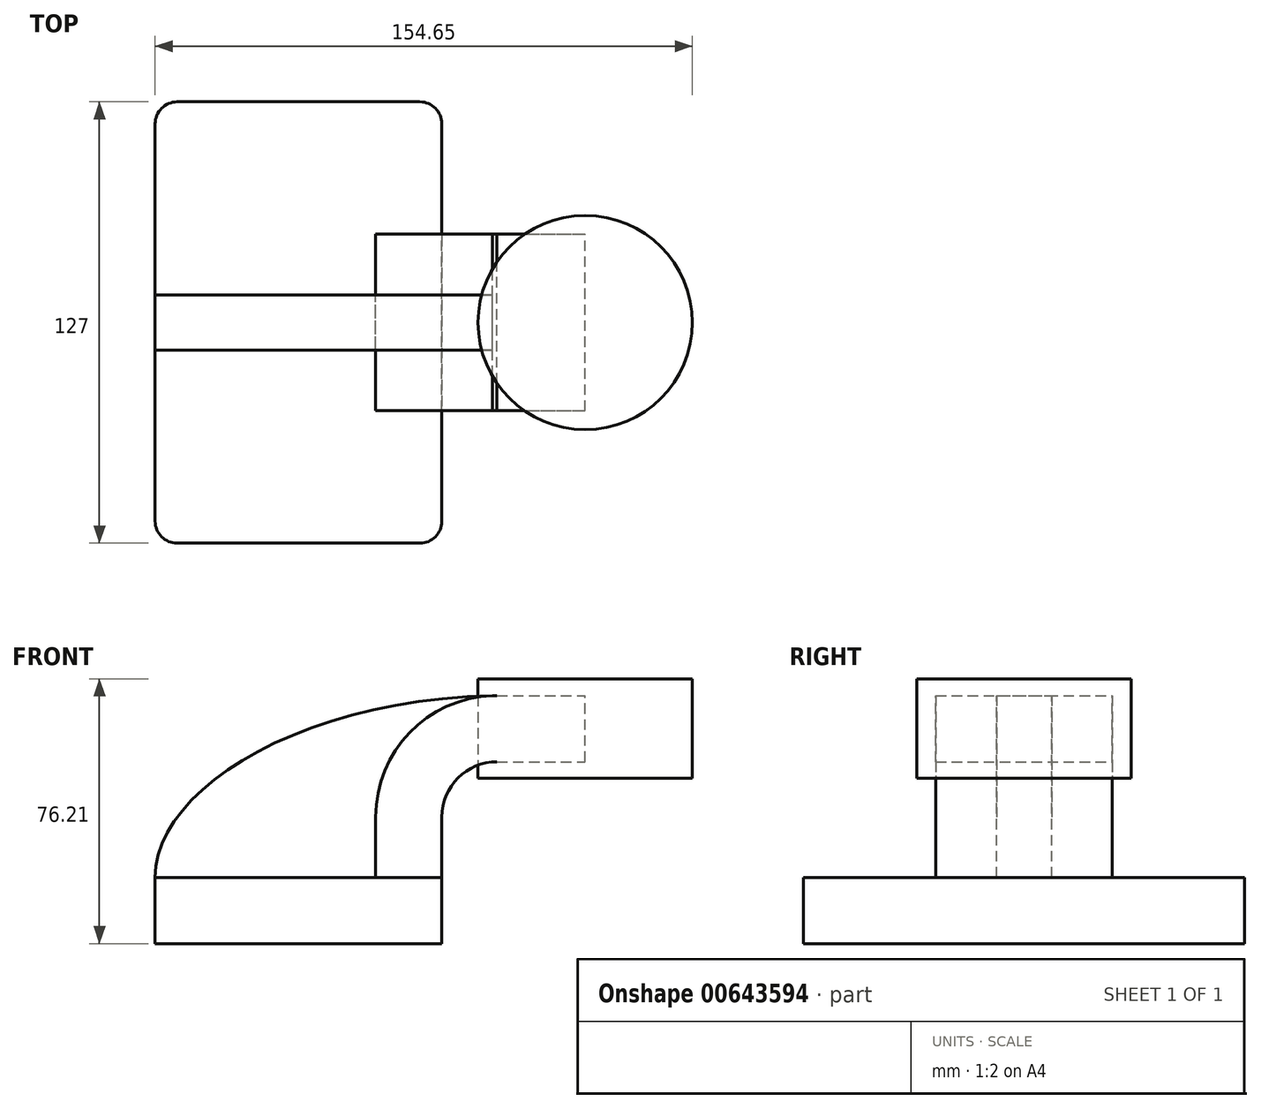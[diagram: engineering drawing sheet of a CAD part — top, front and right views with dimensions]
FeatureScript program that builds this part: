
annotation { "Feature Type Name" : "Feature", "Feature Type Description" : "" }
export const myFeature = defineFeature(function(context is Context, id is Id, definition is map)
    precondition{}
    {
        {
            var Q0;
            Q0=qCreatedBy(makeId("Front.planeOp"),FACE);
            var sketch = newSketch(context, id + "F0", { "sketchPlane" : qUnion([Q0])});
            skLineSegment(sketch, "E0.bottom", {"start": v(-41.28, 9.52) * mm, "end": v(41.27, 9.53) * mm});
            skLineSegment(sketch, "E0.top", {"start": v(-41.28, -9.53) * mm, "end": v(41.28, -9.53) * mm});
            skLineSegment(sketch, "E0.left", {"start": v(-41.28, 9.52) * mm, "end": v(-41.28, -9.53) * mm});
            skLineSegment(sketch, "E0.right", {"start": v(41.27, 9.53) * mm, "end": v(41.28, -9.52) * mm});
            skPoint(sketch, "E0.middle", {"position": v(0, 0) * mm});
            skLineSegment(sketch, "E1.bottom", {"start": v(62.57, 38.1) * mm, "end": v(113.37, 38.1) * mm});
            skLineSegment(sketch, "E1.top", {"start": v(62.57, 66.68) * mm, "end": v(113.37, 66.68) * mm});
            skLineSegment(sketch, "E1.left", {"start": v(62.57, 38.1) * mm, "end": v(62.57, 66.68) * mm});
            skLineSegment(sketch, "E1.right", {"start": v(113.37, 38.1) * mm, "end": v(113.37, 66.68) * mm});
            skPoint(sketch, "E1.middle", {"position": v(87.97, 52.39) * mm});
            skLineSegment(sketch, "E2", {"start": v(41.27, 9.53) * mm, "end": v(41.27, 26.92) * mm});
            skArc(sketch, "E3", {"start": v(41.27, 26.92) * mm, "mid": v(45.92, 38.15) * mm, "end": v(57.15, 42.8) * mm});
            skLineSegment(sketch, "E4", {"start": v(57.15, 42.8) * mm, "end": v(82.53, 42.8) * mm});
            skLineSegment(sketch, "E5.0", {"start": v(57.15, 61.85) * mm, "end": v(82.53, 61.85) * mm});
            skArc(sketch, "E5.1", {"start": v(22.22, 26.92) * mm, "mid": v(32.45, 51.62) * mm, "end": v(57.15, 61.85) * mm});
            skLineSegment(sketch, "E5.2", {"start": v(22.22, 9.53) * mm, "end": v(22.22, 26.92) * mm});
            skLineSegment(sketch, "E6", {"start": v(82.53, 38.1) * mm, "end": v(82.53, 66.68) * mm});
            skFitSpline(sketch, "E7", {"points": [v(-41.28, 9.52) * mm, v(57.15, 61.85) * mm], "startDerivative": vector(-0.56, 74.63) * mm, "endDerivative": vector(171.45, 2.65) * mm});
            skSolve(sketch);
        }
        {
            var Q0;
            Q0=makeQuery(id+"F0.imprint","IMPRINT",FACE,{"disambiguationData":[TD([[makeQuery(id+"F0.imprint","IMPRINT",EDGE,{"derivedFrom":sQuery(id+"F0.wireOp",EDGE,"E0.top")}),1.0]])]});
            extrude(context, id + "F1", {"entities" : qUnion([Q0]), "endBound" : BoundingType.SYMMETRIC, "oppositeDirection" : true, "depth" : 127 * mm, "offsetDistance" : 25.4 * mm});
        }
        {
            var Q0;
            {var subQ1=sQuery(id+"F0.wireOp",EDGE,"E2");Q0=makeQuery(id+"F0.imprint","IMPRINT",FACE,{"disambiguationData":[TD([[makeQuery(id+"F0.imprint","IMPRINT",EDGE,{"derivedFrom":subQ1}),1.0]])]});}
            var Q1;
            {var subQ0=sQuery(id+"F0.wireOp",EDGE,"E4");var subQ1=sQuery(id+"F0.wireOp",EDGE,"E1.left");var subQ2=makeQuery(id+"F0.imprint","INTERSECT",VERTEX,{"derivedFrom":[subQ1,subQ0]});Q1=makeQuery(id+"F0.imprint","IMPRINT",FACE,{"disambiguationData":[TD([[makeQuery(id+"F0.imprint","IMPRINT",EDGE,{"disambiguationData":[TD([[subQ2,-1.0]])],"derivedFrom":subQ1}),-1.0]])]});}
            extrude(context, id + "F2", {"entities" : qUnion([Q0, Q1]), "endBound" : BoundingType.SYMMETRIC, "depth" : 50.8 * mm, "offsetDistance" : 25.4 * mm});
        }
        {
            var Q0;
            {var subQ3=sQuery(id+"F0.wireOp",EDGE,"E5.2");Q0=makeQuery(id+"F0.imprint","IMPRINT",FACE,{"disambiguationData":[TD([[makeQuery(id+"F0.imprint","IMPRINT",EDGE,{"derivedFrom":subQ3}),1.0]])]});}
            extrude(context, id + "F3", {"entities" : qUnion([Q0]), "endBound" : BoundingType.SYMMETRIC, "depth" : 15.88 * mm, "offsetDistance" : 25.4 * mm});
        }
        {
            var Q0;
            {var subQ4=sQuery(id+"F0.wireOp",EDGE,"E1.right");Q0=makeQuery(id+"F0.imprint","IMPRINT",FACE,{"disambiguationData":[TD([[makeQuery(id+"F0.imprint","IMPRINT",EDGE,{"derivedFrom":subQ4}),1.0]])]});}
            var Q1;
            Q1=sQuery(id+"F0.wireOp",EDGE,"E6");
            revolve(context, id + "F4", {"entities" : qUnion([Q0]), "axis" : qUnion([Q1]), "revolveType" : RevolveType.FULL});
        }
        {
            var Q0;
            Q0=makeQuery(id+"F1.opExtrude","CAP_EDGE",EDGE,{"disambiguationData":[OSD([sQuery(id+"F0.wireOp",EDGE,"E0.left")])],"isStart":true});
            var Q1;
            Q1=makeQuery(id+"F1.opExtrude","CAP_EDGE",EDGE,{"disambiguationData":[OSD([sQuery(id+"F0.wireOp",EDGE,"E0.right")])],"isStart":true});
            var Q2;
            Q2=makeQuery(id+"F1.opExtrude","CAP_EDGE",EDGE,{"disambiguationData":[OSD([sQuery(id+"F0.wireOp",EDGE,"E0.right")])],"isStart":false});
            var Q3;
            Q3=makeQuery(id+"F1.opExtrude","CAP_EDGE",EDGE,{"disambiguationData":[OSD([sQuery(id+"F0.wireOp",EDGE,"E0.left")])],"isStart":false});
            fillet(context, id + "F5", {"entities" : qUnion([Q0, Q1, Q2, Q3]), "radius" : 6.35 * mm, "tangentPropagation" : true, "allowEdgeOverflow" : false});
        }
    });
